# Revit family: LBP6
name_source: partatom
category: Lighting Fixtures
revit_build: Autodesk Revit 2014 (Build: 20130308_1515(x64)
units: mm (PartAtom-declared; Revit-internal decimal feet)

## types (1)
- LBP6
    Apparent Load = 0 VA
    Backbox = Hubbell - Aluminium
    Color Filter = 16777215
    Default Elevation = 48"
    Description = LiteBox Plus is an entry level commercial downlight and wall wash targeting distributors and contractors that remain price sensitive to using LEDs for general downlighting applications.
    Dimming Lamp Color Temperature Shift = <None>
    Emit Shape Visible in Rendering = No
    Emit from Circle Diameter = 6"
    Glass = Hubbell- Glass Cover
    Is 120V = Yes
    Is 270V = No
    Lamp = LED Downlight
    Load Classification = Lighting
    Manufacturer = Prescolite Lighting
    Model = LBP6
    Photometric Web File = LBP6_6LBP11L30KWH.IES
    Product Documentation Link = https://hubbellcdn.com
    Product Page URL = https://www.hubbell.com
    Reflector = Hubbell - White
    Tilt Angle = -90.00°
    URL = http://www.prescolite.com
    Voltage = 120 V
    Warranty = 5 year Warranty
    Wattage Comments = 10-20W
    Wire = Hubbell - Wire Finish
    more Photometric Web Link = https://www.hubbell.com

## geometry (parser evidence)
native form markers: Blend x6, Sweep x5
no freeform markers — native parametric forms only
